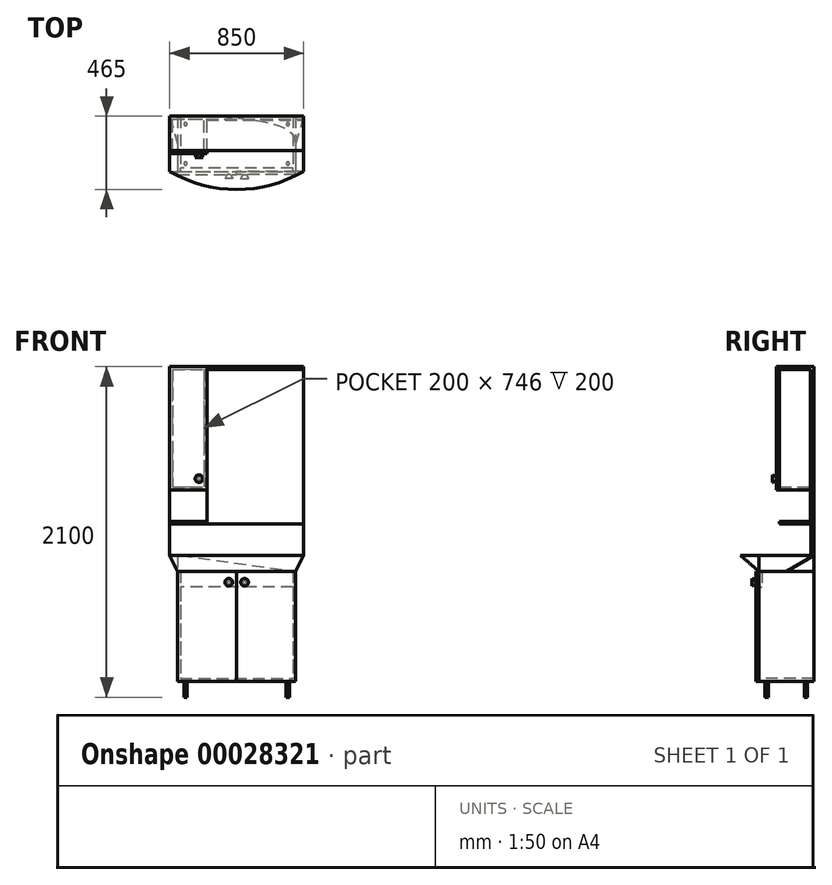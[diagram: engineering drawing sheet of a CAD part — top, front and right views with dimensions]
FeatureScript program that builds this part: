
annotation { "Feature Type Name" : "Feature", "Feature Type Description" : "" }
export const myFeature = defineFeature(function(context is Context, id is Id, definition is map)
    precondition{}
    {
        {
            var Q0;
            Q0=qCreatedBy(makeId("Top.planeOp"),FACE);
            var sketch = newSketch(context, id + "F0", { "sketchPlane" : qUnion([Q0])});
            skLineSegment(sketch, "E0.bottom", {"start": v(-375, 210.27) * mm, "end": v(375, 210.27) * mm});
            skLineSegment(sketch, "E0.top", {"start": v(-375, -139.73) * mm, "end": v(375, -139.73) * mm});
            skLineSegment(sketch, "E0.left", {"start": v(-375, 210.27) * mm, "end": v(-375, -139.73) * mm});
            skLineSegment(sketch, "E0.right", {"start": v(375, 210.27) * mm, "end": v(375, -139.73) * mm});
            skSolve(sketch);
        }
        {
            var Q0;
            Q0=makeQuery(id+"F0.imprint","IMPRINT",FACE,{"disambiguationData":[TD([[makeQuery(id+"F0.imprint","IMPRINT",EDGE,{"derivedFrom":sQuery(id+"F0.wireOp",EDGE,"E0.bottom")}),-1.0]])]});
            extrude(context, id + "F1", {"entities" : qUnion([Q0]), "depth" : 18 * mm});
        }
        {
            var Q0;
            Q0=makeQuery(id+"F1.opExtrude","CAP_FACE",FACE,{"disambiguationData":[OSD([sQuery(id+"F0.wireOp",EDGE,"E0.bottom"),sQuery(id+"F0.wireOp",EDGE,"E0.top"),sQuery(id+"F0.wireOp",EDGE,"E0.left"),sQuery(id+"F0.wireOp",EDGE,"E0.right")])],"isStart":false});
            var sketch = newSketch(context, id + "F2", { "sketchPlane" : qUnion([Q0])});
            skLineSegment(sketch, "E1.bottom", {"start": v(-375, 210.27) * mm, "end": v(-357, 210.27) * mm});
            skLineSegment(sketch, "E1.top", {"start": v(-375, -139.73) * mm, "end": v(-357, -139.73) * mm});
            skLineSegment(sketch, "E1.left", {"start": v(-375, 210.27) * mm, "end": v(-375, -139.73) * mm});
            skLineSegment(sketch, "E1.right", {"start": v(-357, 210.27) * mm, "end": v(-357, -139.73) * mm});
            skLineSegment(sketch, "E2.bottom", {"start": v(375, 210.27) * mm, "end": v(357, 210.27) * mm});
            skLineSegment(sketch, "E2.top", {"start": v(375, -139.73) * mm, "end": v(357, -139.73) * mm});
            skLineSegment(sketch, "E2.left", {"start": v(375, 210.27) * mm, "end": v(375, -139.73) * mm});
            skLineSegment(sketch, "E2.right", {"start": v(357, 210.27) * mm, "end": v(357, -139.73) * mm});
            skSolve(sketch);
        }
        {
            var Q0;
            Q0 = qSketchRegion(id + "F2", true);
            extrude(context, id + "F3", {"entities" : qUnion([Q0]), "operationType" : NewBodyOperationType.ADD, "depth" : 682 * mm});
        }
        {
            var Q0;
            Q0=makeQuery(id+"F3.opExtrude","SWEPT_FACE",FACE,{"disambiguationData":[OSD([sQuery(id+"F2.wireOp",EDGE,"E1.right")])]});
            var sketch = newSketch(context, id + "F4", { "sketchPlane" : qUnion([Q0])});
            skLineSegment(sketch, "E3.bottom", {"start": v(-139.73, 700) * mm, "end": v(-119.73, 700) * mm});
            skLineSegment(sketch, "E3.top", {"start": v(-139.73, 600) * mm, "end": v(-119.73, 600) * mm});
            skLineSegment(sketch, "E3.left", {"start": v(-139.73, 700) * mm, "end": v(-139.73, 600) * mm});
            skLineSegment(sketch, "E3.right", {"start": v(-119.73, 700) * mm, "end": v(-119.73, 600) * mm});
            skSolve(sketch);
        }
        {
            var Q0;
            Q0 = qSketchRegion(id + "F4", true);
            var Q1;
            Q1=makeQuery(id+"F3.opExtrude","SWEPT_FACE",FACE,{"disambiguationData":[OSD([sQuery(id+"F2.wireOp",EDGE,"E2.right")])]});
            extrude(context, id + "F5", {"entities" : qUnion([Q0]), "operationType" : NewBodyOperationType.ADD, "endBound" : BoundingType.UP_TO_SURFACE, "endBoundEntityFace" : qUnion([Q1]), "depth" : 25 * mm});
        }
        {
            var Q0;
            Q0=makeQuery(id+"F5.boolean.opBoolean","MERGE",FACE,{"derivedFrom":[makeQuery(id+"F3.opExtrude","CAP_FACE",FACE,{"disambiguationData":[OSD([sQuery(id+"F2.wireOp",EDGE,"E1.bottom"),sQuery(id+"F2.wireOp",EDGE,"E1.top"),sQuery(id+"F2.wireOp",EDGE,"E1.left"),sQuery(id+"F2.wireOp",EDGE,"E1.right")])],"isStart":false}),makeQuery(id+"F3.opExtrude","CAP_FACE",FACE,{"disambiguationData":[OSD([sQuery(id+"F2.wireOp",EDGE,"E2.bottom"),sQuery(id+"F2.wireOp",EDGE,"E2.top"),sQuery(id+"F2.wireOp",EDGE,"E2.left"),sQuery(id+"F2.wireOp",EDGE,"E2.right")])],"isStart":false}),makeQuery(id+"F5.opExtrude","SWEPT_FACE",FACE,{"disambiguationData":[OSD([sQuery(id+"F4.wireOp",EDGE,"E3.bottom")])]})]});
            cPlane(context, id + "F6", {"entities" : qUnion([Q0]), "cplaneType" : CPlaneType.OFFSET, "offset" : 100 * mm, "width" : 150 * mm, "height" : 150 * mm});
        }
        {
            var Q0;
            Q0=qCreatedBy(id+"F6.planeOp",FACE);
            var sketch = newSketch(context, id + "F7", { "sketchPlane" : qUnion([Q0])});
            skLineSegment(sketch, "E4.0", {"start": v(-375, 210.27) * mm, "end": v(-357, 210.27) * mm});
            skLineSegment(sketch, "E5.bottom", {"start": v(-425, 210.27) * mm, "end": v(425, 210.27) * mm});
            skLineSegment(sketch, "E5.left", {"start": v(-425, 210.27) * mm, "end": v(-425, -139.73) * mm});
            skLineSegment(sketch, "E5.right", {"start": v(425, 210.27) * mm, "end": v(425, -139.73) * mm});
            skPoint(sketch, "E6", {"position": v(0, -254.73) * mm});
            skArc(sketch, "E7", {"start": v(-425, -139.73) * mm, "mid": v(0, -254.73) * mm, "end": v(425, -139.73) * mm});
            skSolve(sketch);
        }
        {
            var Q0;
            Q0=makeQuery(id+"F5.boolean.opBoolean","MERGE",FACE,{"derivedFrom":[makeQuery(id+"F3.opExtrude","CAP_FACE",FACE,{"disambiguationData":[OSD([sQuery(id+"F2.wireOp",EDGE,"E1.bottom"),sQuery(id+"F2.wireOp",EDGE,"E1.top"),sQuery(id+"F2.wireOp",EDGE,"E1.left"),sQuery(id+"F2.wireOp",EDGE,"E1.right")])],"isStart":false}),makeQuery(id+"F3.opExtrude","CAP_FACE",FACE,{"disambiguationData":[OSD([sQuery(id+"F2.wireOp",EDGE,"E2.bottom"),sQuery(id+"F2.wireOp",EDGE,"E2.top"),sQuery(id+"F2.wireOp",EDGE,"E2.left"),sQuery(id+"F2.wireOp",EDGE,"E2.right")])],"isStart":false}),makeQuery(id+"F5.opExtrude","SWEPT_FACE",FACE,{"disambiguationData":[OSD([sQuery(id+"F4.wireOp",EDGE,"E3.bottom")])]})]});
            cPlane(context, id + "F8", {"entities" : qUnion([Q0]), "cplaneType" : CPlaneType.OFFSET, "offset" : 0 * mm, "width" : 150 * mm, "height" : 150 * mm});
        }
        {
            var Q0;
            Q0=qCreatedBy(id+"F8.planeOp",FACE);
            var sketch = newSketch(context, id + "F9", { "sketchPlane" : qUnion([Q0])});
            skLineSegment(sketch, "E8.bottom", {"start": v(-375, 210.27) * mm, "end": v(375, 210.27) * mm});
            skLineSegment(sketch, "E8.top", {"start": v(-375, -139.73) * mm, "end": v(375, -139.73) * mm});
            skLineSegment(sketch, "E8.left", {"start": v(-375, 210.27) * mm, "end": v(-375, -139.73) * mm});
            skLineSegment(sketch, "E8.right", {"start": v(375, 210.27) * mm, "end": v(375, -139.73) * mm});
            skPoint(sketch, "E9.0", {"position": v(-375, 210.27) * mm});
            skPoint(sketch, "E10.0", {"position": v(-375, -139.73) * mm});
            skPoint(sketch, "E11.0", {"position": v(375, -139.73) * mm});
            skSolve(sketch);
        }
        {
            var Q0;
            {var subQ1=sQuery(id+"F7.wireOp",EDGE,"E5.left");Q0=makeQuery(id+"F7.imprint","IMPRINT",FACE,{"disambiguationData":[TD([[makeQuery(id+"F7.imprint","IMPRINT",EDGE,{"derivedFrom":subQ1}),1.0]])]});}
            var Q1;
            Q1=makeQuery(id+"F9.imprint","IMPRINT",FACE,{"disambiguationData":[TD([[makeQuery(id+"F9.imprint","IMPRINT",EDGE,{"derivedFrom":sQuery(id+"F9.wireOp",EDGE,"E8.bottom")}),-1.0]])]});
            loft(context, id + "F10", {"sheetProfilesArray" : [{ "sheetProfileEntities" : qUnion([Q0]) }, { "sheetProfileEntities" : qUnion([Q1]) }]});
        }
        {
            var Q0;
            Q0=qCreatedBy(id+"F6.planeOp",FACE);
            var sketch = newSketch(context, id + "F11", { "sketchPlane" : qUnion([Q0])});
            skLineSegment(sketch, "E12.bottom", {"start": v(-425, 210.27) * mm, "end": v(425, 210.27) * mm});
            skLineSegment(sketch, "E12.top", {"start": v(-425, 192.27) * mm, "end": v(425, 192.27) * mm});
            skLineSegment(sketch, "E12.left", {"start": v(-425, 210.27) * mm, "end": v(-425, 192.27) * mm});
            skLineSegment(sketch, "E12.right", {"start": v(425, 210.27) * mm, "end": v(425, 192.27) * mm});
            skPoint(sketch, "E13.0", {"position": v(-425, 210.27) * mm});
            skPoint(sketch, "E14.0", {"position": v(425, 210.27) * mm});
            skSolve(sketch);
        }
        {
            var Q0;
            Q0=makeQuery(id+"F11.imprint","IMPRINT",FACE,{"disambiguationData":[TD([[makeQuery(id+"F11.imprint","IMPRINT",EDGE,{"derivedFrom":sQuery(id+"F11.wireOp",EDGE,"E12.bottom")}),-1.0]])]});
            extrude(context, id + "F12", {"entities" : qUnion([Q0]), "depth" : 1200 * mm});
        }
        {
            var Q0;
            Q0=makeQuery(id+"F12.opExtrude","SWEPT_FACE",FACE,{"disambiguationData":[OSD([sQuery(id+"F11.wireOp",EDGE,"E12.top")])]});
            var sketch = newSketch(context, id + "F13", { "sketchPlane" : qUnion([Q0])});
            skLineSegment(sketch, "E15.bottom", {"start": v(-425, 2000) * mm, "end": v(425, 2000) * mm});
            skLineSegment(sketch, "E15.top", {"start": v(-425, 1982) * mm, "end": v(425, 1982) * mm});
            skLineSegment(sketch, "E15.left", {"start": v(-425, 2000) * mm, "end": v(-425, 1982) * mm});
            skLineSegment(sketch, "E15.right", {"start": v(425, 2000) * mm, "end": v(425, 1982) * mm});
            skLineSegment(sketch, "E16.bottom", {"start": v(-425, 1982) * mm, "end": v(-189, 1982) * mm});
            skLineSegment(sketch, "E16.top", {"start": v(-425, 1218) * mm, "end": v(-189, 1218) * mm});
            skLineSegment(sketch, "E16.left", {"start": v(-425, 1982) * mm, "end": v(-425, 1218) * mm});
            skLineSegment(sketch, "E16.right", {"start": v(-189, 1982) * mm, "end": v(-189, 1218) * mm});
            skLineSegment(sketch, "E17.bottom", {"start": v(-407, 1982) * mm, "end": v(-207, 1982) * mm});
            skLineSegment(sketch, "E17.top", {"start": v(-407, 1236) * mm, "end": v(-207, 1236) * mm});
            skLineSegment(sketch, "E17.left", {"start": v(-407, 1982) * mm, "end": v(-407, 1236) * mm});
            skLineSegment(sketch, "E17.right", {"start": v(-207, 1982) * mm, "end": v(-207, 1236) * mm});
            skLineSegment(sketch, "E18.bottom", {"start": v(-425, 1018) * mm, "end": v(-189, 1018) * mm});
            skLineSegment(sketch, "E18.top", {"start": v(-425, 1000) * mm, "end": v(-189, 1000) * mm});
            skLineSegment(sketch, "E18.left", {"start": v(-425, 1018) * mm, "end": v(-425, 1000) * mm});
            skLineSegment(sketch, "E18.right", {"start": v(-189, 1018) * mm, "end": v(-189, 1000) * mm});
            skSolve(sketch);
        }
        {
            var Q0;
            Q0 = qSketchRegion(id + "F13", true);
            extrude(context, id + "F14", {"entities" : qUnion([Q0]), "operationType" : NewBodyOperationType.ADD, "depth" : 200 * mm});
        }
        {
            var Q0;
            {var subQ0=sQuery(id+"F11.wireOp",EDGE,"E12.top");var subQ2=sQuery(id+"F11.wireOp",EDGE,"E12.left");Q0=makeQuery(id+"F14.boolean.opBoolean","SPLIT",FACE,{"disambiguationData":[TD([makeQuery(id+"F12.opExtrude","SWEPT_FACE",FACE,{"disambiguationData":[OSD([subQ2])]})])],"derivedFrom":makeQuery(id+"F12.opExtrude","SWEPT_FACE",FACE,{"disambiguationData":[OSD([subQ0])]})});}
            var sketch = newSketch(context, id + "F15", { "sketchPlane" : qUnion([Q0])});
            skLineSegment(sketch, "E19.bottom", {"start": v(-189, 1982) * mm, "end": v(425, 1982) * mm});
            skLineSegment(sketch, "E19.top", {"start": v(-189, 1000) * mm, "end": v(425, 1000) * mm});
            skLineSegment(sketch, "E19.left", {"start": v(-189, 1982) * mm, "end": v(-189, 1000) * mm});
            skLineSegment(sketch, "E19.right", {"start": v(425, 1982) * mm, "end": v(425, 1000) * mm});
            skSolve(sketch);
        }
        {
            var Q0;
            {var subQ5=sQuery(id+"F15.wireOp",EDGE,"E19.bottom");Q0=makeQuery(id+"F15.imprint","IMPRINT",FACE,{"disambiguationData":[TD([[makeQuery(id+"F15.imprint","IMPRINT",EDGE,{"derivedFrom":subQ5}),-1.0]])]});}
            extrude(context, id + "F16", {"entities" : qUnion([Q0]), "depth" : 5 * mm});
        }
        {
            var Q0;
            Q0=makeQuery(id+"F1.opExtrude","CAP_FACE",FACE,{"disambiguationData":[OSD([sQuery(id+"F0.wireOp",EDGE,"E0.bottom"),sQuery(id+"F0.wireOp",EDGE,"E0.top"),sQuery(id+"F0.wireOp",EDGE,"E0.left"),sQuery(id+"F0.wireOp",EDGE,"E0.right")])],"isStart":true});
            var sketch = newSketch(context, id + "F17", { "sketchPlane" : qUnion([Q0])});
            skCircle(sketch, "E20", {"center": v(-325, 89.73) * mm, "radius": 10 * mm});
            skLineSegment(sketch, "E21.0", {"start": v(0, -210.27) * mm, "end": v(0, 139.73) * mm});
            skLineSegment(sketch, "E22.0", {"start": v(-383.44, -35.27) * mm, "end": v(366.56, -35.27) * mm});
            skCircle(sketch, "E23.MirrorC", {"center": v(325, 89.73) * mm, "radius": 10 * mm});
            skCircle(sketch, "E24.MirrorC", {"center": v(-325, -160.27) * mm, "radius": 10 * mm});
            skCircle(sketch, "E25.MirrorC", {"center": v(325, -160.27) * mm, "radius": 10 * mm});
            skSolve(sketch);
        }
        {
            var Q0;
            Q0 = qSketchRegion(id + "F17", true);
            extrude(context, id + "F18", {"entities" : qUnion([Q0]), "operationType" : NewBodyOperationType.ADD, "depth" : 100 * mm});
        }
        {
            var Q0;
            Q0=makeQuery(id+"F14.opExtrude","CAP_FACE",FACE,{"disambiguationData":[OSD([sQuery(id+"F13.wireOp",EDGE,"E15.bottom"),sQuery(id+"F13.wireOp",EDGE,"E15.top"),sQuery(id+"F13.wireOp",EDGE,"E15.left"),sQuery(id+"F13.wireOp",EDGE,"E15.right"),sQuery(id+"F13.wireOp",EDGE,"E16.top"),sQuery(id+"F13.wireOp",EDGE,"E16.left"),sQuery(id+"F13.wireOp",EDGE,"E16.right"),sQuery(id+"F13.wireOp",EDGE,"E17.bottom"),sQuery(id+"F13.wireOp",EDGE,"E17.top"),sQuery(id+"F13.wireOp",EDGE,"E17.left"),sQuery(id+"F13.wireOp",EDGE,"E17.right")])],"isStart":false});
            cPlane(context, id + "F19", {"entities" : qUnion([Q0]), "cplaneType" : CPlaneType.OFFSET, "offset" : 1 * mm, "width" : 150 * mm, "height" : 150 * mm});
        }
        {
            var Q0;
            Q0=qCreatedBy(id+"F19.planeOp",FACE);
            var sketch = newSketch(context, id + "F20", { "sketchPlane" : qUnion([Q0])});
            skPoint(sketch, "E26.0", {"position": v(-425, 2000) * mm});
            skPoint(sketch, "E27.0", {"position": v(-189, 1218) * mm});
            skLineSegment(sketch, "E28.bottom", {"start": v(-425, 2000) * mm, "end": v(-189, 2000) * mm});
            skLineSegment(sketch, "E28.top", {"start": v(-425, 1218) * mm, "end": v(-189, 1218) * mm});
            skLineSegment(sketch, "E28.left", {"start": v(-425, 2000) * mm, "end": v(-425, 1218) * mm});
            skLineSegment(sketch, "E28.right", {"start": v(-189, 2000) * mm, "end": v(-189, 1218) * mm});
            skSolve(sketch);
        }
        {
            var Q0;
            Q0 = qSketchRegion(id + "F20", true);
            extrude(context, id + "F21", {"entities" : qUnion([Q0]), "operationType" : NewBodyOperationType.ADD, "depth" : 18 * mm});
        }
        {
            var Q0;
            Q0=makeQuery(id+"F21.opExtrude","CAP_FACE",FACE,{"disambiguationData":[OSD([sQuery(id+"F20.wireOp",EDGE,"E28.bottom"),sQuery(id+"F20.wireOp",EDGE,"E28.top"),sQuery(id+"F20.wireOp",EDGE,"E28.left"),sQuery(id+"F20.wireOp",EDGE,"E28.right")])],"isStart":false});
            var sketch = newSketch(context, id + "F22", { "sketchPlane" : qUnion([Q0])});
            skCircle(sketch, "E29", {"center": v(-239, 1288) * mm, "radius": 10 * mm});
            skSolve(sketch);
        }
        {
            var Q0;
            Q0 = qSketchRegion(id + "F22", true);
            extrude(context, id + "F23", {"entities" : qUnion([Q0]), "operationType" : NewBodyOperationType.ADD, "depth" : 25 * mm, "hasDraft" : true, "draftAngle" : 30 * degree});
        }
        {
            var Q0;
            Q0=makeQuery(id+"F5.boolean.opBoolean","MERGE",FACE,{"derivedFrom":[makeQuery(id+"F3.boolean.opBoolean","MERGE",FACE,{"derivedFrom":[makeQuery(id+"F1.opExtrude","SWEPT_FACE",FACE,{"disambiguationData":[OSD([sQuery(id+"F0.wireOp",EDGE,"E0.top")])]}),makeQuery(id+"F3.opExtrude","SWEPT_FACE",FACE,{"disambiguationData":[OSD([sQuery(id+"F2.wireOp",EDGE,"E1.top")])]}),makeQuery(id+"F3.opExtrude","SWEPT_FACE",FACE,{"disambiguationData":[OSD([sQuery(id+"F2.wireOp",EDGE,"E2.top")])]})]}),makeQuery(id+"F5.opExtrude","SWEPT_FACE",FACE,{"disambiguationData":[OSD([sQuery(id+"F4.wireOp",EDGE,"E3.left")])]})]});
            cPlane(context, id + "F24", {"entities" : qUnion([Q0]), "cplaneType" : CPlaneType.OFFSET, "offset" : 1 * mm, "width" : 150 * mm, "height" : 150 * mm});
        }
        {
            var Q0;
            Q0=qCreatedBy(id+"F24.planeOp",FACE);
            var sketch = newSketch(context, id + "F25", { "sketchPlane" : qUnion([Q0])});
            skPoint(sketch, "E30.0", {"position": v(-375, 700) * mm});
            skPoint(sketch, "E31.0", {"position": v(0, 0) * mm});
            skLineSegment(sketch, "E32.bottom", {"start": v(-375, 700) * mm, "end": v(0, 700) * mm});
            skLineSegment(sketch, "E32.top", {"start": v(-375, 0) * mm, "end": v(0, 0) * mm});
            skLineSegment(sketch, "E32.left", {"start": v(-375, 700) * mm, "end": v(-375, 0) * mm});
            skLineSegment(sketch, "E32.right", {"start": v(0, 700) * mm, "end": v(0, 0) * mm});
            skSolve(sketch);
        }
        {
            var Q0;
            Q0 = qSketchRegion(id + "F25", true);
            extrude(context, id + "F26", {"entities" : qUnion([Q0]), "depth" : 18 * mm});
        }
        {
            var Q0;
            Q0=makeQuery(id+"F26.opExtrude","CAP_FACE",FACE,{"disambiguationData":[OSD([sQuery(id+"F25.wireOp",EDGE,"E32.bottom"),sQuery(id+"F25.wireOp",EDGE,"E32.top"),sQuery(id+"F25.wireOp",EDGE,"E32.left"),sQuery(id+"F25.wireOp",EDGE,"E32.right")])],"isStart":false});
            var sketch = newSketch(context, id + "F27", { "sketchPlane" : qUnion([Q0])});
            skCircle(sketch, "E33", {"center": v(-50, 630) * mm, "radius": 10 * mm});
            skSolve(sketch);
        }
        {
            var Q0;
            Q0 = qSketchRegion(id + "F27", true);
            extrude(context, id + "F28", {"entities" : qUnion([Q0]), "operationType" : NewBodyOperationType.ADD, "depth" : 25 * mm, "hasDraft" : true, "draftAngle" : 30 * degree});
        }
        {
            var Q0;
            Q0=makeQuery(id+"F26.opExtrude","SWEPT_BODY",BODY,{"disambiguationData":[OSD([sQuery(id+"F25.wireOp",EDGE,"E32.bottom"),sQuery(id+"F25.wireOp",EDGE,"E32.top"),sQuery(id+"F25.wireOp",EDGE,"E32.left"),sQuery(id+"F25.wireOp",EDGE,"E32.right")])]});
            var Q1;
            Q1=qCreatedBy(makeId("Right.planeOp"),FACE);
            mirror(context, id + "F29", {"entities" : qUnion([Q0]), "mirrorPlane" : qUnion([Q1])});
        }
    });
